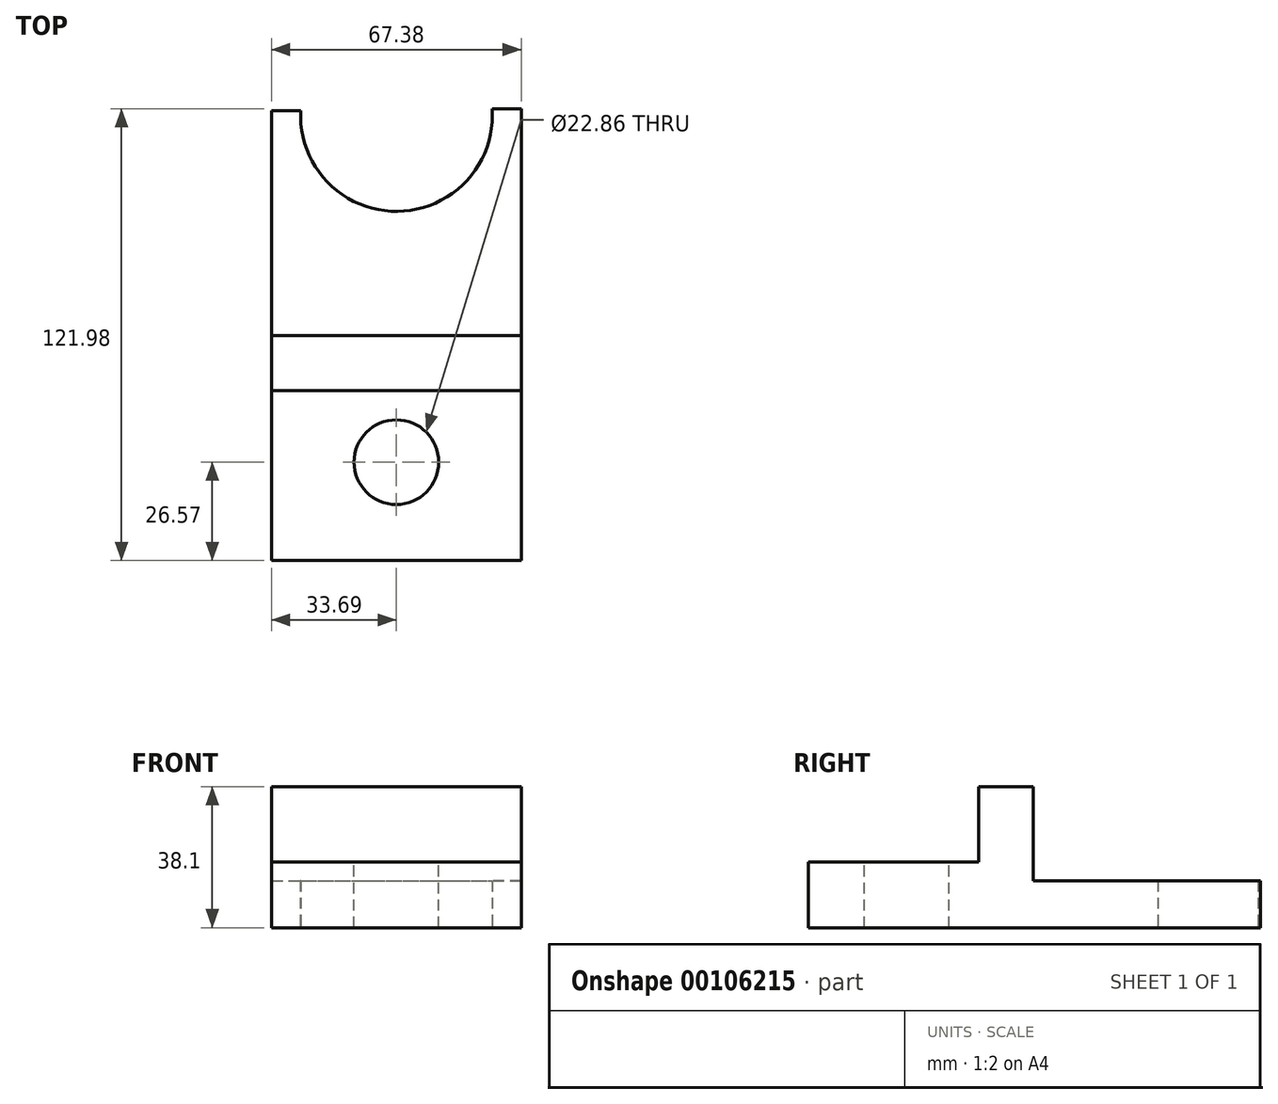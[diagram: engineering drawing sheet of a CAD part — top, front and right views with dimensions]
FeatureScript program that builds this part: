
annotation { "Feature Type Name" : "Feature", "Feature Type Description" : "" }
export const myFeature = defineFeature(function(context is Context, id is Id, definition is map)
    precondition{}
    {
        {
            var Q0;
            Q0=qCreatedBy(makeId("Top.planeOp"),FACE);
            var sketch = newSketch(context, id + "F0", { "sketchPlane" : qUnion([Q0])});
            skLineSegment(sketch, "E0", {"start": v(-33.69, -55.9) * mm, "end": v(33.69, -55.9) * mm});
            skLineSegment(sketch, "E1", {"start": v(33.69, -55.9) * mm, "end": v(33.69, 66.07) * mm});
            skLineSegment(sketch, "E2", {"start": v(33.69, 66.07) * mm, "end": v(25.85, 66.07) * mm});
            skLineSegment(sketch, "E3", {"start": v(-33.69, -55.9) * mm, "end": v(-33.69, 65.49) * mm});
            skLineSegment(sketch, "E4", {"start": v(-33.69, 65.49) * mm, "end": v(-25.85, 65.49) * mm});
            skArc(sketch, "E5", {"start": v(-25.85, 65.49) * mm, "mid": v(0.3, 38.36) * mm, "end": v(25.85, 66.07) * mm});
            skSolve(sketch);
        }
        {
            var Q0;
            Q0 = qSketchRegion(id + "F0", true);
            extrude(context, id + "F1", {"entities" : qUnion([Q0]), "depth" : 12.7 * mm});
        }
        {
            var Q0;
            Q0=makeQuery(id+"F1.opExtrude","CAP_FACE",FACE,{"disambiguationData":[OSD([sQuery(id+"F0.wireOp",EDGE,"E0"),sQuery(id+"F0.wireOp",EDGE,"E1"),sQuery(id+"F0.wireOp",EDGE,"E2"),sQuery(id+"F0.wireOp",EDGE,"E3"),sQuery(id+"F0.wireOp",EDGE,"E4"),sQuery(id+"F0.wireOp",EDGE,"E5")])],"isStart":false});
            var sketch = newSketch(context, id + "F2", { "sketchPlane" : qUnion([Q0])});
            skLineSegment(sketch, "E6", {"start": v(-33.69, 4.8) * mm, "end": v(33.69, 4.8) * mm});
            skPoint(sketch, "E6.endSnap0", {"position": v(-33.69, 4.8) * mm});
            skLineSegment(sketch, "E7", {"start": v(33.69, 4.8) * mm, "end": v(33.69, -10.02) * mm});
            skLineSegment(sketch, "E8", {"start": v(33.69, -10.02) * mm, "end": v(-33.69, -10.02) * mm});
            skLineSegment(sketch, "E9", {"start": v(-33.69, -10.02) * mm, "end": v(-33.69, 4.8) * mm});
            skSolve(sketch);
        }
        {
            var Q0;
            Q0 = qSketchRegion(id + "F2", true);
            extrude(context, id + "F3", {"entities" : qUnion([Q0]), "operationType" : NewBodyOperationType.ADD, "depth" : 25.4 * mm});
        }
        {
            var Q0;
            {var subQ0=sQuery(id+"F0.wireOp",EDGE,"E3");var subQ1=sQuery(id+"F0.wireOp",EDGE,"E1");var subQ2=sQuery(id+"F0.wireOp",EDGE,"E0");Q0=makeQuery(id+"F3.boolean.opBoolean","SPLIT",FACE,{"disambiguationData":[TD([makeQuery(id+"F1.opExtrude","SWEPT_FACE",FACE,{"disambiguationData":[OSD([subQ2])]})])],"derivedFrom":makeQuery(id+"F1.opExtrude","CAP_FACE",FACE,{"disambiguationData":[OSD([subQ2,subQ1,sQuery(id+"F0.wireOp",EDGE,"E2"),subQ0,sQuery(id+"F0.wireOp",EDGE,"E4"),sQuery(id+"F0.wireOp",EDGE,"E5")])],"isStart":false})});}
            var sketch = newSketch(context, id + "F4", { "sketchPlane" : qUnion([Q0])});
            skLineSegment(sketch, "E10", {"start": v(-33.69, -55.9) * mm, "end": v(-33.69, -10.02) * mm});
            skLineSegment(sketch, "E11", {"start": v(-33.69, -10.02) * mm, "end": v(33.69, -10.02) * mm});
            skLineSegment(sketch, "E12", {"start": v(33.69, -10.02) * mm, "end": v(33.69, -55.9) * mm});
            skLineSegment(sketch, "E13", {"start": v(33.69, -55.9) * mm, "end": v(-33.69, -55.9) * mm});
            skSolve(sketch);
        }
        {
            var Q0;
            Q0 = qSketchRegion(id + "F4", true);
            extrude(context, id + "F5", {"entities" : qUnion([Q0]), "operationType" : NewBodyOperationType.ADD, "depth" : 5.08 * mm});
        }
        {
            var Q0;
            Q0=makeQuery(id+"F5.opExtrude","CAP_FACE",FACE,{"disambiguationData":[OSD([sQuery(id+"F4.wireOp",EDGE,"E10"),sQuery(id+"F4.wireOp",EDGE,"E11"),sQuery(id+"F4.wireOp",EDGE,"E12"),sQuery(id+"F4.wireOp",EDGE,"E13")])],"isStart":false});
            var sketch = newSketch(context, id + "F6", { "sketchPlane" : qUnion([Q0])});
            skCircle(sketch, "E14", {"center": v(0, -29.34) * mm, "radius": 9.4 * mm});
            skSolve(sketch);
        }
        {
            var Q0;
            Q0=sQuery(id+"F6.wireOp",VERTEX,"E14.center");
            var Q1;
            Q1=makeQuery(id+"F1.opExtrude","SWEPT_BODY",BODY,{"disambiguationData":[OSD([sQuery(id+"F0.wireOp",EDGE,"E0"),sQuery(id+"F0.wireOp",EDGE,"E1"),sQuery(id+"F0.wireOp",EDGE,"E2"),sQuery(id+"F0.wireOp",EDGE,"E3"),sQuery(id+"F0.wireOp",EDGE,"E4"),sQuery(id+"F0.wireOp",EDGE,"E5")])]});
            hole(context, id + "F7", {"style" : HoleStyle.SIMPLE, "endStyle" : HoleEndStyle.THROUGH, "holeDiameter" : 22.86 * mm, "locations" : qUnion([Q0]), "scope" : qUnion([Q1]), "isTappedThrough" : true});
        }
    });
